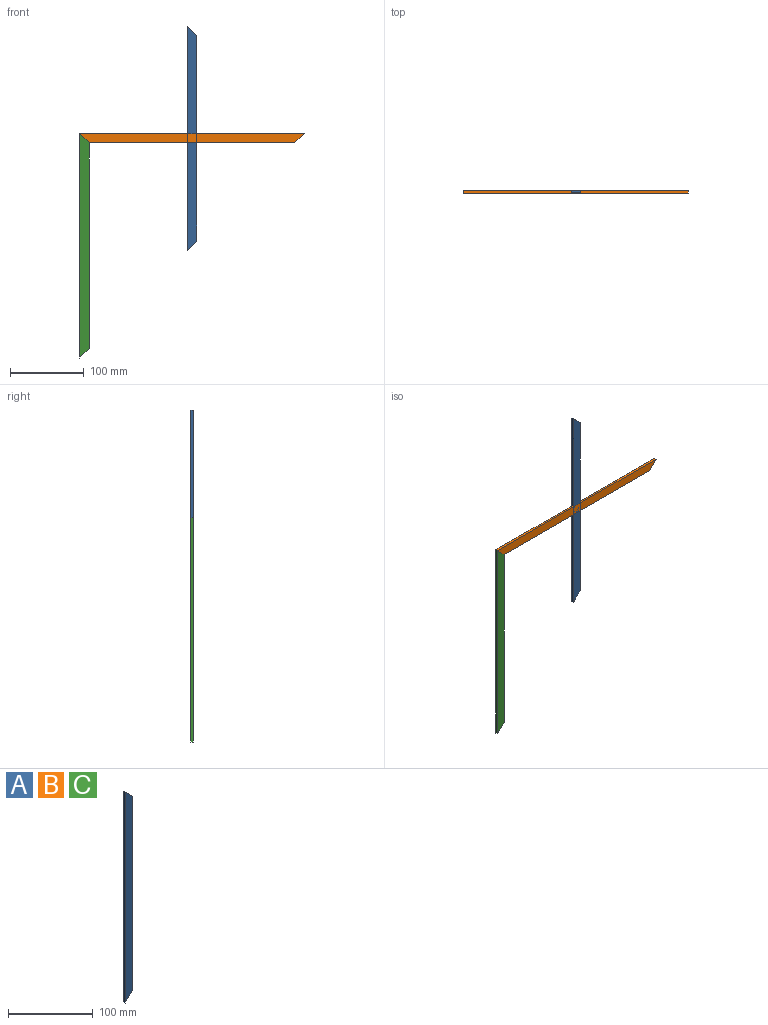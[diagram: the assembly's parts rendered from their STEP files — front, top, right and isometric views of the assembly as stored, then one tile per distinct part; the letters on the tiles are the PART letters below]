
ASSEMBLY  parts=3 mates=1
PART A: 6 faces, bbox 12.7x3.2x304.8 mm
  f0: plane 12.7x12.7mm, normal (0.71,0,0.71), area 57mm2, adj f1,f3,f4,f5
  f1: plane 304.8x3.18mm, normal (-1,0,0), area 967.7mm2, adj f0,f2,f4,f5
  f2: plane 12.7x12.7mm, normal (0.71,0,-0.71), area 57mm2, adj f1,f3,f4,f5
  f3: plane 279.4x3.18mm, normal (1,0,0), area 887.1mm2, adj f0,f2,f4,f5
  f4: plane 304.8x12.7mm, normal (0,-1,0), area 3709.7mm2, adj f0,f1,f2,f3
  f5: plane 304.8x12.7mm, normal (0,1,0), area 3709.7mm2, adj f0,f1,f2,f3
PART B: same geometry as A
PART C: same geometry as A
PLACE A t=(57.43,-8.9,131.93)mm
PLACE B rot(axis=(-0.71,0,0.71),180deg) t=(56.92,-12.08,131.41)mm
PLACE C t=(-88.71,-8.9,-14.21)mm
MATE fastened B.f0 <-> C.f0  axis (-0.71,0,-0.71) through (-95.06,-10.49,137.76)mm
